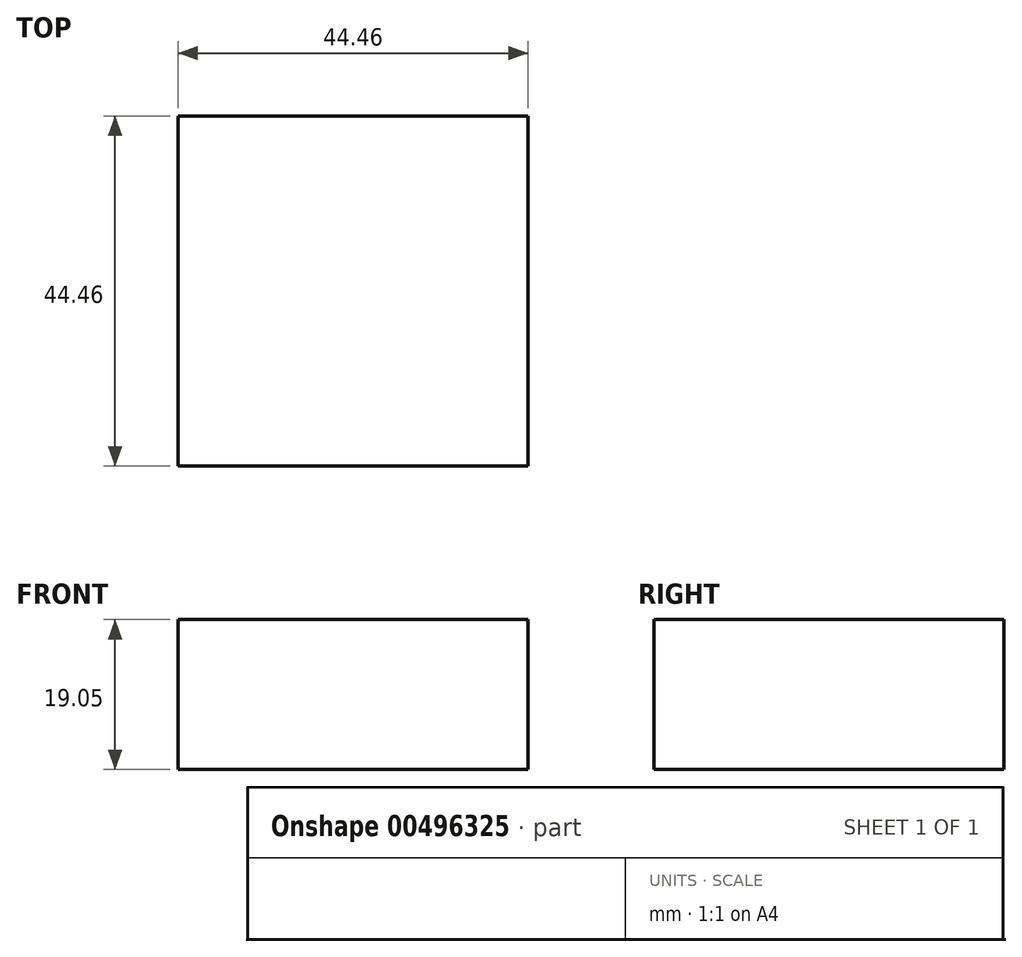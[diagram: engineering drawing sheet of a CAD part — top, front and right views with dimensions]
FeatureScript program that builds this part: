
annotation { "Feature Type Name" : "Feature", "Feature Type Description" : "" }
export const myFeature = defineFeature(function(context is Context, id is Id, definition is map)
    precondition{}
    {
        {
            var Q0;
            Q0=qCreatedBy(makeId("Top.planeOp"),FACE);
            var sketch = newSketch(context, id + "F0", { "sketchPlane" : qUnion([Q0])});
            skLineSegment(sketch, "E0.bottom", {"start": v(22.22, -22.23) * mm, "end": v(-22.23, -22.23) * mm});
            skLineSegment(sketch, "E0.top", {"start": v(22.23, 22.23) * mm, "end": v(-22.23, 22.22) * mm});
            skLineSegment(sketch, "E0.left", {"start": v(22.22, -22.23) * mm, "end": v(22.23, 22.23) * mm});
            skLineSegment(sketch, "E0.right", {"start": v(-22.23, -22.23) * mm, "end": v(-22.23, 22.22) * mm});
            skPoint(sketch, "E0.middle", {"position": v(0, 0) * mm});
            skSolve(sketch);
        }
        {
            var Q0;
            Q0 = qSketchRegion(id + "F0", true);
            extrude(context, id + "F1", {"entities" : qUnion([Q0]), "depth" : 19.05 * mm});
        }
    });
